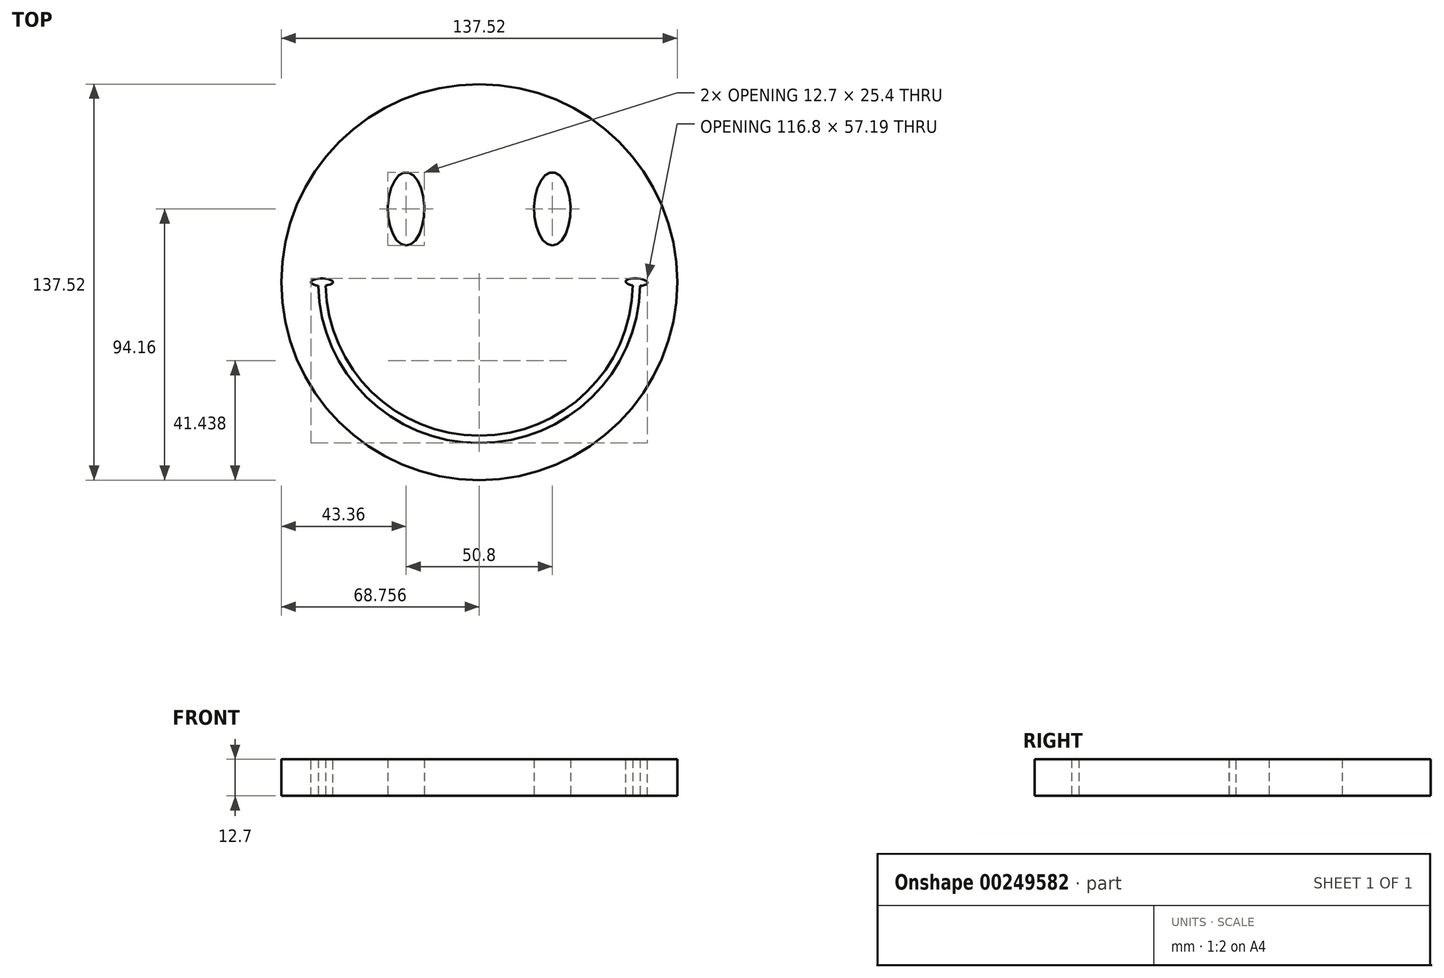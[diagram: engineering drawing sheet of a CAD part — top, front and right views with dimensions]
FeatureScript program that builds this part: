
annotation { "Feature Type Name" : "Feature", "Feature Type Description" : "" }
export const myFeature = defineFeature(function(context is Context, id is Id, definition is map)
    precondition{}
    {
        {
            var Q0;
            Q0=qCreatedBy(makeId("Top.planeOp"),FACE);
            var sketch = newSketch(context, id + "F0", { "sketchPlane" : qUnion([Q0])});
            skCircle(sketch, "E0", {"center": v(0, 0) * mm, "radius": 68.76 * mm});
            skArc(sketch, "E1", {"start": v(-55.9, -1.2) * mm, "mid": v(-0.04, -55.92) * mm, "end": v(55.9, -1.27) * mm});
            skLineSegment(sketch, "E2", {"start": v(0, 0) * mm, "end": v(25.4, 0) * mm});
            skLineSegment(sketch, "E3", {"start": v(25.4, 0) * mm, "end": v(25.4, 25.4) * mm});
            skLineSegment(sketch, "E4", {"start": v(25.4, 25.4) * mm, "end": v(-25.4, 25.4) * mm});
            skEllipse(sketch, "E5", {"center": v(-25.4, 25.4) * mm, "majorRadius": 12.7 * mm, "minorRadius": 6.35 * mm, "majorAxis": v(0, -1)});
            skEllipse(sketch, "E6", {"center": v(25.4, 25.4) * mm, "majorRadius": 12.7 * mm, "minorRadius": 6.35 * mm, "majorAxis": v(0, -1)});
            skArc(sketch, "E7.0", {"start": v(-53.36, -1.2) * mm, "mid": v(0.04, -53.38) * mm, "end": v(53.36, -1.12) * mm});
            skEllipse(sketch, "E8", {"center": v(-54.65, 0) * mm, "majorRadius": 3.81 * mm, "minorRadius": 1.27 * mm, "majorAxis": v(1, 0)});
            skPoint(sketch, "E9.orphan", {"position": v(-55.92, 0) * mm});
            skPoint(sketch, "E10.orphan", {"position": v(-53.38, 0) * mm});
            skEllipse(sketch, "E11", {"center": v(54.65, 0) * mm, "majorRadius": 3.81 * mm, "minorRadius": 1.27 * mm, "majorAxis": v(1, -0.07)});
            skPoint(sketch, "E12.start.orphan", {"position": v(53.38, 0) * mm});
            skPoint(sketch, "E13.orphan", {"position": v(55.92, 0) * mm});
            skSolve(sketch);
        }
        {
            var Q0;
            Q0=makeQuery(id+"F0.imprint","IMPRINT",FACE,{"disambiguationData":[TD([[makeQuery(id+"F0.imprint","IMPRINT",EDGE,{"derivedFrom":sQuery(id+"F0.wireOp",EDGE,"E0")}),1.0]])]});
            extrude(context, id + "F1", {"entities" : qUnion([Q0]), "depth" : 12.7 * mm});
        }
    });
